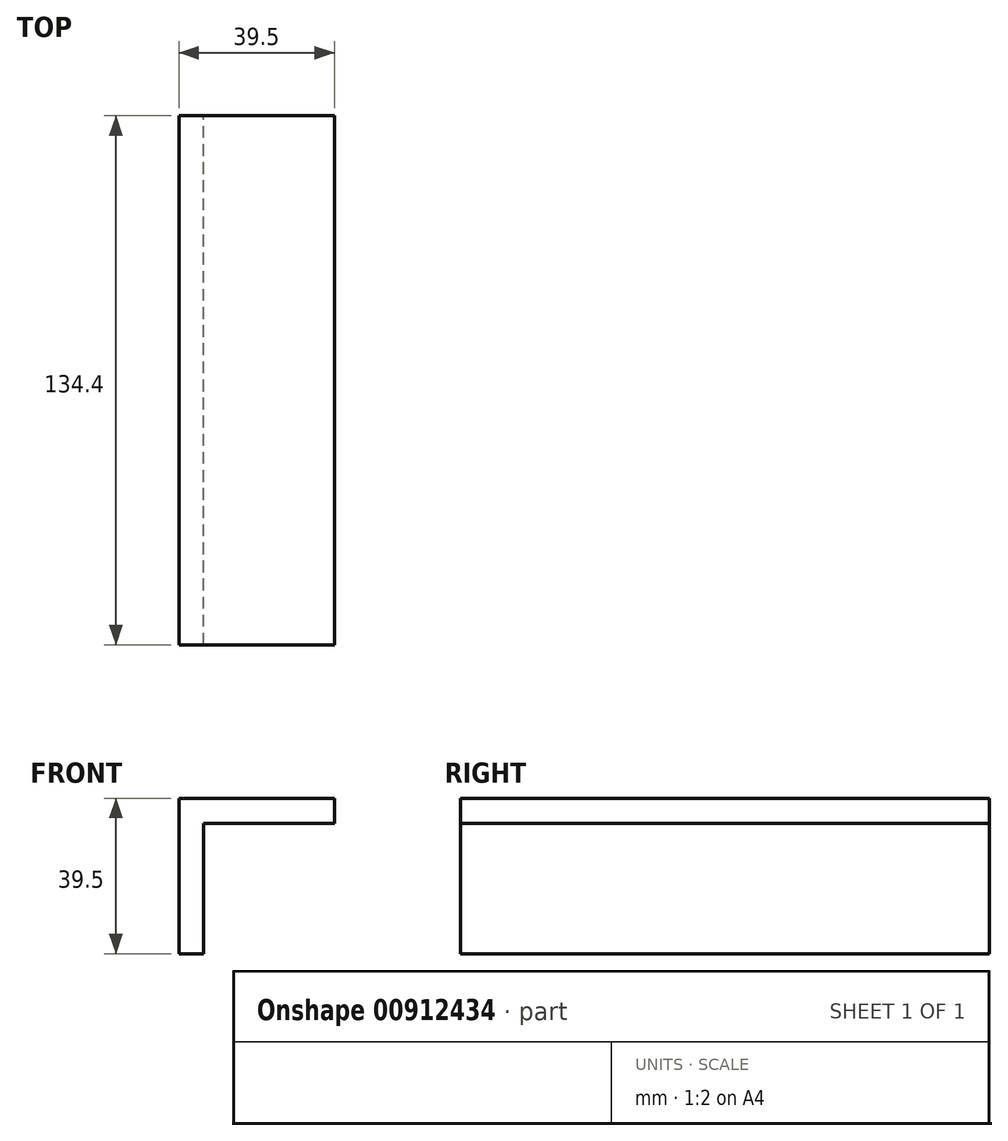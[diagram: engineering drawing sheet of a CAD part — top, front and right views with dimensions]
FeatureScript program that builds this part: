
annotation { "Feature Type Name" : "Feature", "Feature Type Description" : "" }
export const myFeature = defineFeature(function(context is Context, id is Id, definition is map)
    precondition{}
    {
        {
            var Q0;
            Q0=qCreatedBy(makeId("Front.planeOp"),FACE);
            var sketch = newSketch(context, id + "F0", { "sketchPlane" : qUnion([Q0])});
            skLineSegment(sketch, "E0", {"start": v(0.08, 0) * mm, "end": v(0.08, 39.5) * mm});
            skLineSegment(sketch, "E1", {"start": v(0.08, 39.5) * mm, "end": v(39.58, 39.5) * mm});
            skLineSegment(sketch, "E2", {"start": v(39.58, 39.5) * mm, "end": v(39.58, 33.15) * mm});
            skLineSegment(sketch, "E3", {"start": v(39.58, 33.15) * mm, "end": v(6.35, 33.15) * mm});
            skLineSegment(sketch, "E4", {"start": v(6.35, 33.15) * mm, "end": v(6.35, 0) * mm});
            skLineSegment(sketch, "E5", {"start": v(6.35, 0) * mm, "end": v(0, 0) * mm});
            skSolve(sketch);
        }
        {
            var Q0;
            Q0 = qSketchRegion(id + "F0", true);
            extrude(context, id + "F1", {"entities" : qUnion([Q0]), "depth" : 134.4 * mm, "offsetDistance" : 25 * mm});
        }
    });
